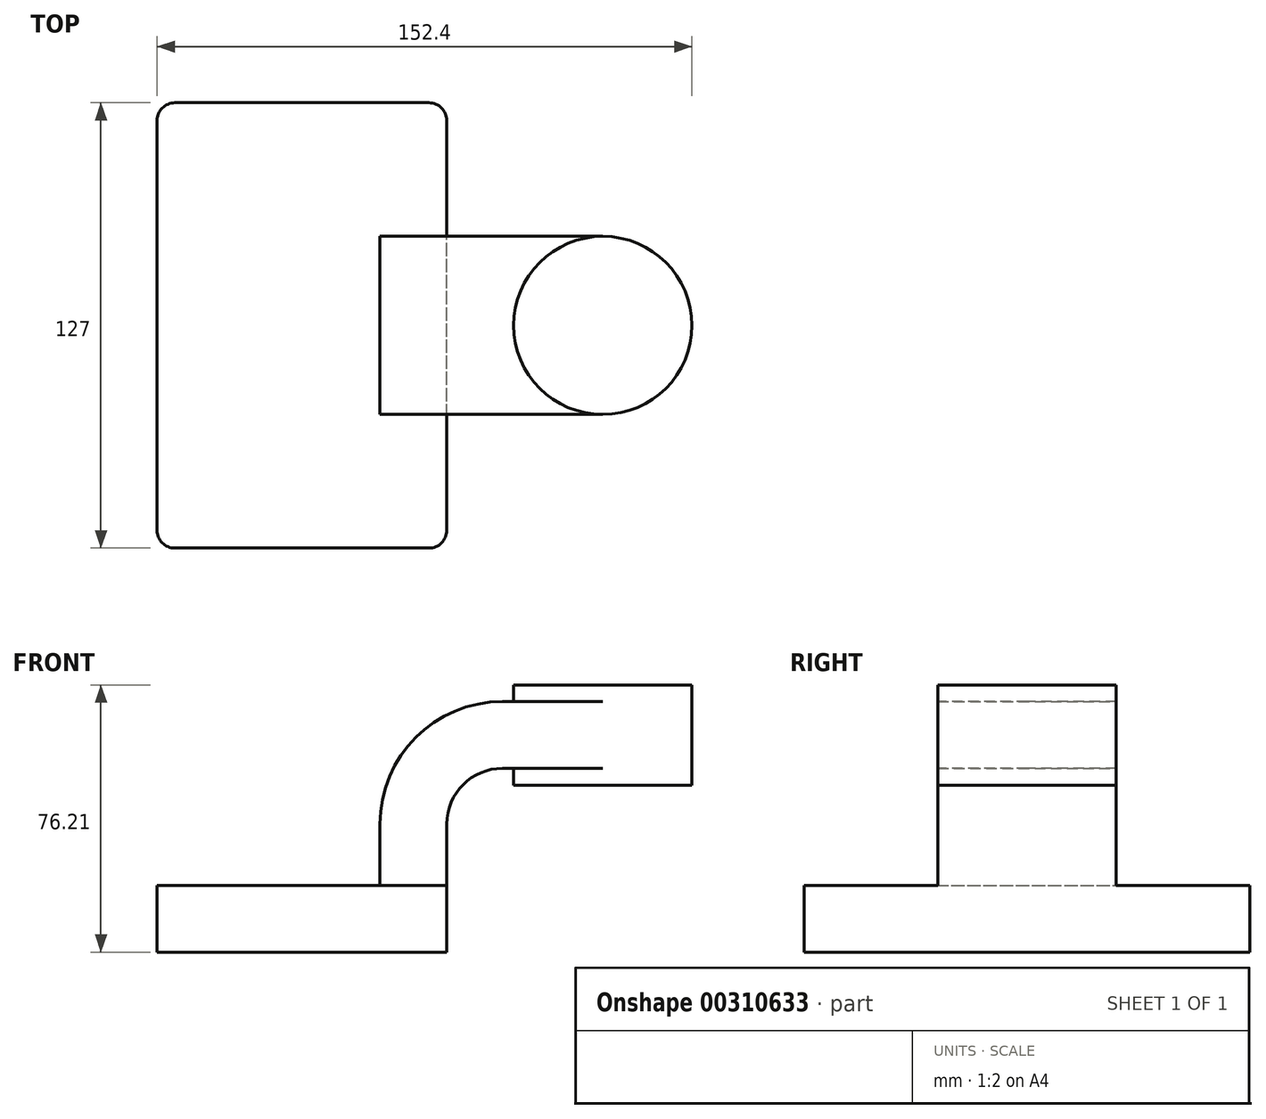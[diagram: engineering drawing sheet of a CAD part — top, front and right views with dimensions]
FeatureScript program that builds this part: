
annotation { "Feature Type Name" : "Feature", "Feature Type Description" : "" }
export const myFeature = defineFeature(function(context is Context, id is Id, definition is map)
    precondition{}
    {
        {
            var Q0;
            Q0=qCreatedBy(makeId("Front.planeOp"),FACE);
            var sketch = newSketch(context, id + "F0", { "sketchPlane" : qUnion([Q0])});
            skLineSegment(sketch, "E0.bottom", {"start": v(-41.28, 9.52) * mm, "end": v(41.28, 9.53) * mm});
            skLineSegment(sketch, "E0.top", {"start": v(-41.28, -9.52) * mm, "end": v(41.28, -9.52) * mm});
            skLineSegment(sketch, "E0.left", {"start": v(-41.28, 9.52) * mm, "end": v(-41.27, -9.53) * mm});
            skLineSegment(sketch, "E0.right", {"start": v(41.28, 9.53) * mm, "end": v(41.28, -9.52) * mm});
            skPoint(sketch, "E0.middle", {"position": v(0, 0) * mm});
            skLineSegment(sketch, "E1.bottom", {"start": v(60.33, 66.67) * mm, "end": v(111.13, 66.67) * mm});
            skLineSegment(sketch, "E1.top", {"start": v(60.33, 38.1) * mm, "end": v(111.13, 38.1) * mm});
            skLineSegment(sketch, "E1.left", {"start": v(60.33, 66.67) * mm, "end": v(60.33, 38.1) * mm});
            skLineSegment(sketch, "E1.right", {"start": v(111.13, 66.67) * mm, "end": v(111.13, 38.1) * mm});
            skPoint(sketch, "E1.middle", {"position": v(85.73, 52.39) * mm});
            skLineSegment(sketch, "E2", {"start": v(41.27, 9.53) * mm, "end": v(41.27, 27) * mm});
            skArc(sketch, "E3", {"start": v(41.27, 27) * mm, "mid": v(45.92, 38.23) * mm, "end": v(57.15, 42.88) * mm});
            skLineSegment(sketch, "E4", {"start": v(57.15, 42.88) * mm, "end": v(85.73, 42.88) * mm});
            skLineSegment(sketch, "E5.0", {"start": v(57.15, 61.93) * mm, "end": v(85.73, 61.93) * mm});
            skArc(sketch, "E5.1", {"start": v(22.23, 27) * mm, "mid": v(32.45, 51.7) * mm, "end": v(57.15, 61.93) * mm});
            skLineSegment(sketch, "E5.2", {"start": v(22.22, 9.53) * mm, "end": v(22.22, 27) * mm});
            skLineSegment(sketch, "E6", {"start": v(85.73, 38.1) * mm, "end": v(85.73, 66.67) * mm});
            skFitSpline(sketch, "E7", {"points": [v(57.15, 61.93) * mm, v(-41.28, 9.53) * mm], "startDerivative": vector(-113.54, 1.17) * mm, "endDerivative": vector(-48.75, -130.8) * mm});
            skSolve(sketch);
        }
        {
            var Q0;
            Q0=makeQuery(id+"F0.imprint","IMPRINT",FACE,{"disambiguationData":[TD([[makeQuery(id+"F0.imprint","IMPRINT",EDGE,{"derivedFrom":sQuery(id+"F0.wireOp",EDGE,"E0.top")}),1.0]])]});
            extrude(context, id + "F1", {"entities" : qUnion([Q0]), "endBound" : BoundingType.SYMMETRIC, "depth" : 127 * mm});
        }
        {
            var Q0;
            {var subQ1=sQuery(id+"F0.wireOp",EDGE,"E2");Q0=makeQuery(id+"F0.imprint","IMPRINT",FACE,{"disambiguationData":[TD([[makeQuery(id+"F0.imprint","IMPRINT",EDGE,{"derivedFrom":subQ1}),1.0]])]});}
            extrude(context, id + "F2", {"entities" : qUnion([Q0]), "operationType" : NewBodyOperationType.ADD, "endBound" : BoundingType.SYMMETRIC, "depth" : 50.8 * mm});
        }
        {
            var Q0;
            Q0=makeQuery(id+"F0.imprint","IMPRINT",FACE,{"disambiguationData":[TD([[makeQuery(id+"F0.imprint","IMPRINT",EDGE,{"derivedFrom":sQuery(id+"F0.wireOp",EDGE,"E5.1")}),1.0]])]});
            extrude(context, id + "F3", {"entities" : qUnion([Q0]), "operationType" : NewBodyOperationType.ADD, "endBound" : BoundingType.SYMMETRIC, "depth" : 15.88 * mm});
        }
        {
            var Q0;
            {var subQ0=sQuery(id+"F0.wireOp",EDGE,"E1.right");Q0=makeQuery(id+"F0.imprint","IMPRINT",FACE,{"disambiguationData":[TD([[makeQuery(id+"F0.imprint","IMPRINT",EDGE,{"derivedFrom":subQ0}),-1.0]])]});}
            var Q1;
            Q1=sQuery(id+"F0.wireOp",EDGE,"E6");
            revolve(context, id + "F4", {"operationType" : NewBodyOperationType.ADD, "entities" : qUnion([Q0]), "axis" : qUnion([Q1]), "revolveType" : RevolveType.FULL});
        }
        {
            var Q0;
            {var subQ0=sQuery(id+"F0.wireOp",EDGE,"E5.0");var subQ1=sQuery(id+"F0.wireOp",EDGE,"E1.left");var subQ2=makeQuery(id+"F0.imprint","INTERSECT",VERTEX,{"derivedFrom":[subQ1,subQ0]});Q0=makeQuery(id+"F0.imprint","IMPRINT",FACE,{"disambiguationData":[TD([[makeQuery(id+"F0.imprint","IMPRINT",EDGE,{"disambiguationData":[TD([[subQ2,-1.0]])],"derivedFrom":subQ1}),1.0]])]});}
            extrude(context, id + "F5", {"entities" : qUnion([Q0]), "operationType" : NewBodyOperationType.ADD, "endBound" : BoundingType.SYMMETRIC, "depth" : 50.8 * mm});
        }
        {
            var Q0;
            Q0=makeQuery(id+"F1.opExtrude","CAP_EDGE",EDGE,{"disambiguationData":[OSD([sQuery(id+"F0.wireOp",EDGE,"E0.right")])],"isStart":false});
            var Q1;
            Q1=makeQuery(id+"F1.opExtrude","CAP_EDGE",EDGE,{"disambiguationData":[OSD([sQuery(id+"F0.wireOp",EDGE,"E0.left")])],"isStart":false});
            var Q2;
            Q2=makeQuery(id+"F1.opExtrude","CAP_EDGE",EDGE,{"disambiguationData":[OSD([sQuery(id+"F0.wireOp",EDGE,"E0.right")])],"isStart":true});
            var Q3;
            Q3=makeQuery(id+"F1.opExtrude","CAP_EDGE",EDGE,{"disambiguationData":[OSD([sQuery(id+"F0.wireOp",EDGE,"E0.left")])],"isStart":true});
            fillet(context, id + "F6", {"entities" : qUnion([Q0, Q1, Q2, Q3]), "radius" : 5.08 * mm, "tangentPropagation" : true, "allowEdgeOverflow" : false});
        }
    });
